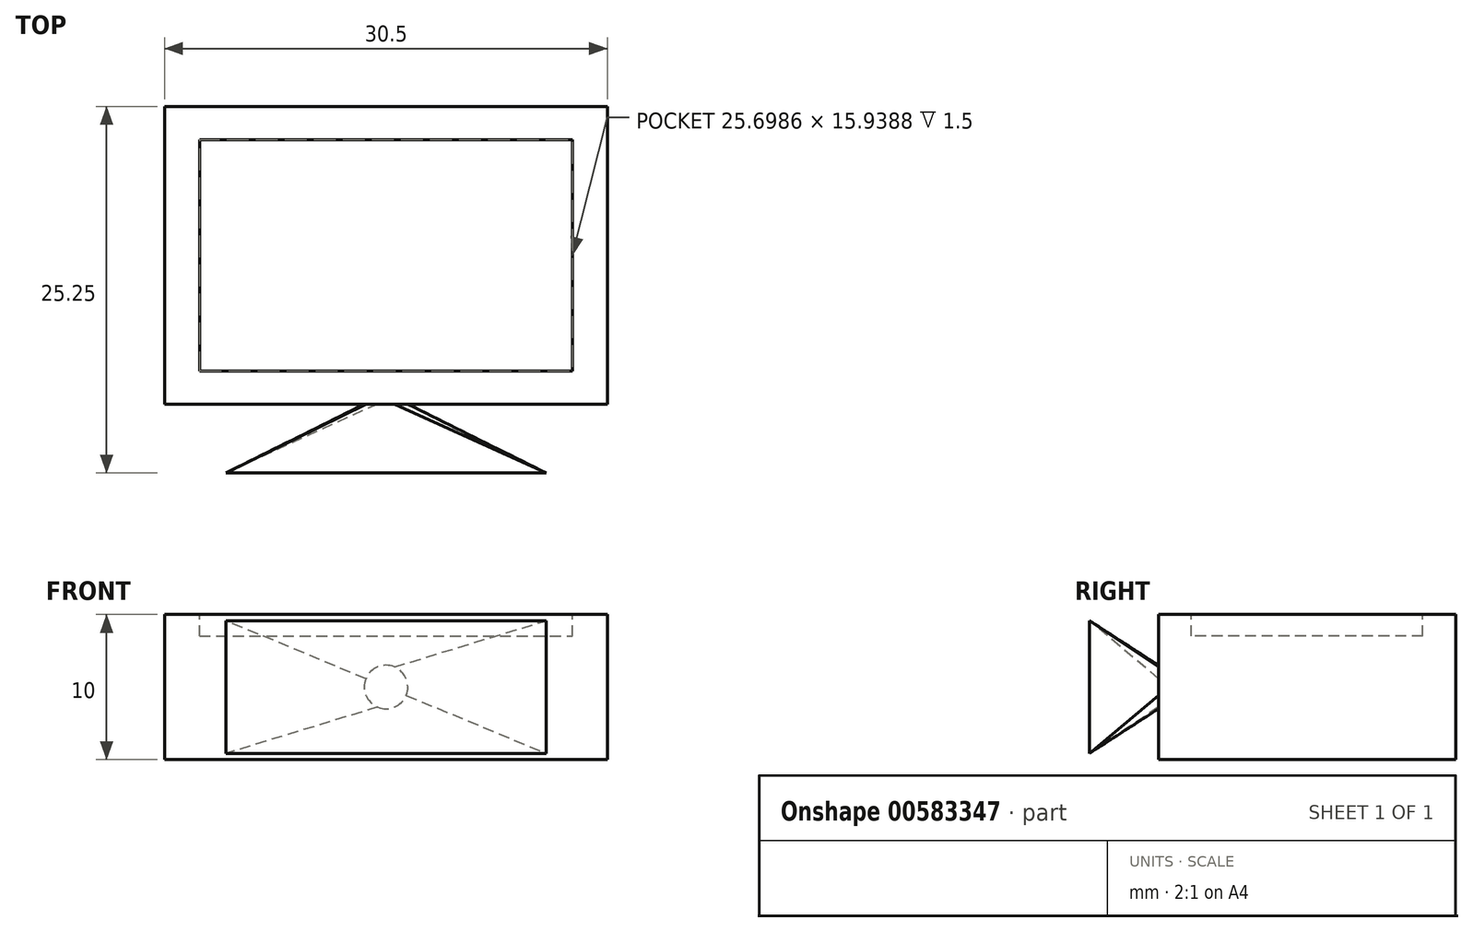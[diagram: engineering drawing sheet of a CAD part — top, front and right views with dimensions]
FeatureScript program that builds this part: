
annotation { "Feature Type Name" : "Feature", "Feature Type Description" : "" }
export const myFeature = defineFeature(function(context is Context, id is Id, definition is map)
    precondition{}
    {
        {
            var Q0;
            Q0=qCreatedBy(makeId("Top.planeOp"),FACE);
            var sketch = newSketch(context, id + "F0", { "sketchPlane" : qUnion([Q0])});
            skLineSegment(sketch, "E0.bottom", {"start": v(-15.25, 10.25) * mm, "end": v(15.25, 10.25) * mm});
            skLineSegment(sketch, "E0.top", {"start": v(-15.25, -10.25) * mm, "end": v(15.25, -10.25) * mm});
            skLineSegment(sketch, "E0.left", {"start": v(-15.25, 10.25) * mm, "end": v(-15.25, -10.25) * mm});
            skLineSegment(sketch, "E0.right", {"start": v(15.25, 10.25) * mm, "end": v(15.25, -10.25) * mm});
            skPoint(sketch, "E0.middle", {"position": v(0, 0) * mm});
            skSolve(sketch);
        }
        {
            var Q0;
            Q0 = qSketchRegion(id + "F0", true);
            extrude(context, id + "F1", {"entities" : qUnion([Q0]), "depth" : 10 * mm, "offsetDistance" : 25 * mm});
        }
        {
            var Q0;
            Q0=makeQuery(id+"F1.opExtrude","CAP_FACE",FACE,{"disambiguationData":[OSD([sQuery(id+"F0.wireOp",EDGE,"E0.bottom"),sQuery(id+"F0.wireOp",EDGE,"E0.top"),sQuery(id+"F0.wireOp",EDGE,"E0.left"),sQuery(id+"F0.wireOp",EDGE,"E0.right")])],"isStart":false});
            var sketch = newSketch(context, id + "F2", { "sketchPlane" : qUnion([Q0])});
            skLineSegment(sketch, "E1.bottom", {"start": v(-12.85, 7.97) * mm, "end": v(12.85, 7.97) * mm});
            skLineSegment(sketch, "E1.top", {"start": v(-12.85, -7.97) * mm, "end": v(12.85, -7.97) * mm});
            skLineSegment(sketch, "E1.left", {"start": v(-12.85, 7.97) * mm, "end": v(-12.85, -7.97) * mm});
            skLineSegment(sketch, "E1.right", {"start": v(12.85, 7.97) * mm, "end": v(12.85, -7.97) * mm});
            skPoint(sketch, "E1.middle", {"position": v(0, 0) * mm});
            skSolve(sketch);
        }
        {
            var Q0;
            Q0 = qSketchRegion(id + "F2", true);
            extrude(context, id + "F3", {"entities" : qUnion([Q0]), "operationType" : NewBodyOperationType.REMOVE, "oppositeDirection" : true, "depth" : 1.5 * mm, "offsetDistance" : 25 * mm});
        }
        {
            var Q0;
            Q0=makeQuery(id+"F1.opExtrude","SWEPT_FACE",FACE,{"disambiguationData":[OSD([sQuery(id+"F0.wireOp",EDGE,"E0.top")])]});
            var sketch = newSketch(context, id + "F4", { "sketchPlane" : qUnion([Q0])});
            skLineSegment(sketch, "E2", {"start": v(0, 5) * mm, "end": v(-1.5, 5) * mm});
            skPoint(sketch, "E2.startSnap0", {"position": v(15.25, 5) * mm});
            skCircle(sketch, "E3", {"center": v(0, 5) * mm, "radius": 1.5 * mm});
            skSolve(sketch);
        }
        {
            var Q0;
            Q0=qCreatedBy(makeId("Front.planeOp"),FACE);
            cPlane(context, id + "F5", {"entities" : qUnion([Q0]), "cplaneType" : CPlaneType.OFFSET, "offset" : 15 * mm, "width" : 150 * mm, "height" : 150 * mm});
        }
        {
            var Q0;
            Q0=qCreatedBy(id+"F5.planeOp",FACE);
            var sketch = newSketch(context, id + "F6", { "sketchPlane" : qUnion([Q0])});
            skLineSegment(sketch, "E4.bottom", {"start": v(-11.03, 9.57) * mm, "end": v(11.03, 9.57) * mm});
            skLineSegment(sketch, "E4.top", {"start": v(-11.03, 0.43) * mm, "end": v(11.03, 0.43) * mm});
            skLineSegment(sketch, "E4.left", {"start": v(-11.03, 9.57) * mm, "end": v(-11.03, 0.43) * mm});
            skLineSegment(sketch, "E4.right", {"start": v(11.03, 9.57) * mm, "end": v(11.03, 0.43) * mm});
            skPoint(sketch, "E4.middle", {"position": v(0, 5) * mm});
            skSolve(sketch);
        }
        {
            var Q1;
            Q1=makeQuery(id+"F4.imprint","IMPRINT",FACE,{"disambiguationData":[TD([[makeQuery(id+"F4.imprint","IMPRINT",EDGE,{"derivedFrom":sQuery(id+"F4.wireOp",EDGE,"E3")}),1.0]])]});
            var Q2;
            Q2=makeQuery(id+"F6.imprint","IMPRINT",FACE,{"disambiguationData":[TD([[makeQuery(id+"F6.imprint","IMPRINT",EDGE,{"derivedFrom":sQuery(id+"F6.wireOp",EDGE,"E4.bottom")}),-1.0]])]});
            loft(context, id + "F7", {"operationType" : NewBodyOperationType.ADD, "sheetProfilesArray" : [{ "sheetProfileEntities" : qUnion([Q1]) }, { "sheetProfileEntities" : qUnion([Q2]) }]});
        }
    });
